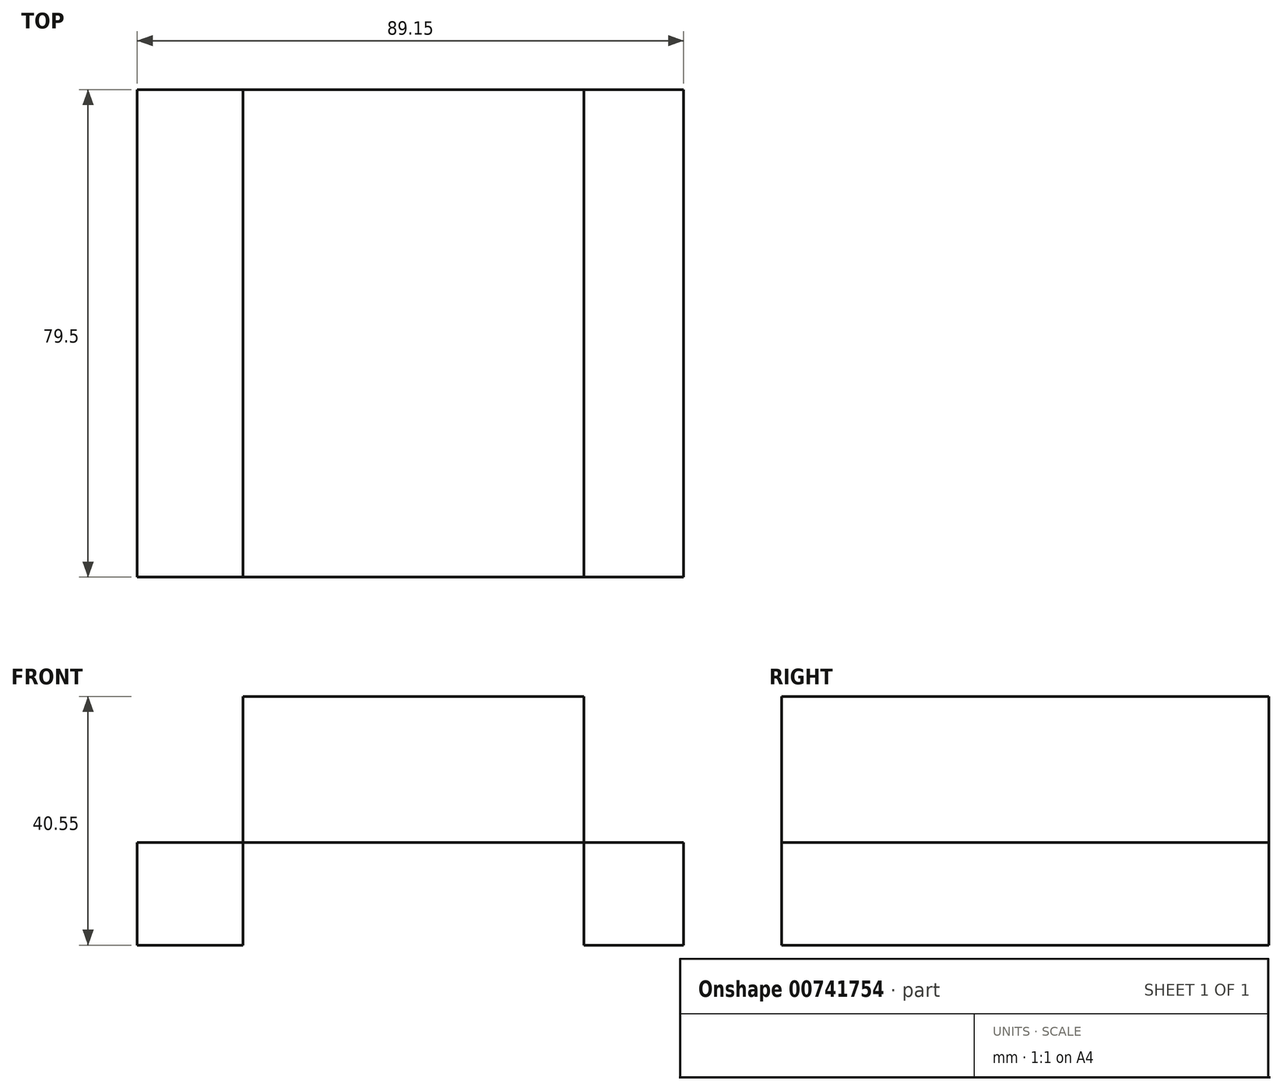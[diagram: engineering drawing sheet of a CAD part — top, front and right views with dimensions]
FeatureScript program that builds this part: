
annotation { "Feature Type Name" : "Feature", "Feature Type Description" : "" }
export const myFeature = defineFeature(function(context is Context, id is Id, definition is map)
    precondition{}
    {
        {
            var Q0;
            Q0=qCreatedBy(makeId("Front.planeOp"),FACE);
            var sketch = newSketch(context, id + "F0", { "sketchPlane" : qUnion([Q0])});
            skLineSegment(sketch, "E0", {"start": v(44.32, 0) * mm, "end": v(44.32, 16.76) * mm});
            skLineSegment(sketch, "E1", {"start": v(44.32, 16.76) * mm, "end": v(28.07, 16.76) * mm});
            skLineSegment(sketch, "E2", {"start": v(28.07, 16.76) * mm, "end": v(28.07, 40.55) * mm});
            skLineSegment(sketch, "E3", {"start": v(28.07, 40.55) * mm, "end": v(-27.56, 40.55) * mm});
            skLineSegment(sketch, "E4", {"start": v(-27.56, 40.55) * mm, "end": v(-27.56, 16.76) * mm});
            skLineSegment(sketch, "E5", {"start": v(-27.56, 16.76) * mm, "end": v(-44.83, 16.76) * mm});
            skLineSegment(sketch, "E6", {"start": v(-44.83, 16.76) * mm, "end": v(-44.83, 0) * mm});
            skLineSegment(sketch, "E7", {"start": v(-44.83, 0) * mm, "end": v(-27.56, 0) * mm});
            skLineSegment(sketch, "E8", {"start": v(-27.56, 0) * mm, "end": v(-27.56, 16.76) * mm});
            skLineSegment(sketch, "E9", {"start": v(-27.56, 16.76) * mm, "end": v(28.07, 16.76) * mm});
            skLineSegment(sketch, "E10", {"start": v(28.07, 0) * mm, "end": v(44.32, 0) * mm});
            skLineSegment(sketch, "E11", {"start": v(28.07, 0) * mm, "end": v(28.07, 16.76) * mm});
            skSolve(sketch);
        }
        {
            var Q0;
            Q0=makeQuery(id+"F0.imprint","IMPRINT",FACE,{"disambiguationData":[TD([[makeQuery(id+"F0.imprint","IMPRINT",EDGE,{"derivedFrom":sQuery(id+"F0.wireOp",EDGE,"E5")}),1.0]])]});
            var Q1;
            Q1=makeQuery(id+"F0.imprint","IMPRINT",FACE,{"disambiguationData":[TD([[makeQuery(id+"F0.imprint","IMPRINT",EDGE,{"derivedFrom":sQuery(id+"F0.wireOp",EDGE,"E2")}),1.0]])]});
            var Q2;
            Q2=makeQuery(id+"F0.imprint","IMPRINT",FACE,{"disambiguationData":[TD([[makeQuery(id+"F0.imprint","IMPRINT",EDGE,{"derivedFrom":sQuery(id+"F0.wireOp",EDGE,"E0")}),1.0]])]});
            extrude(context, id + "F1", {"entities" : qUnion([Q0, Q1, Q2]), "depth" : 79.5 * mm, "offsetDistance" : 25.4 * mm});
        }
    });
